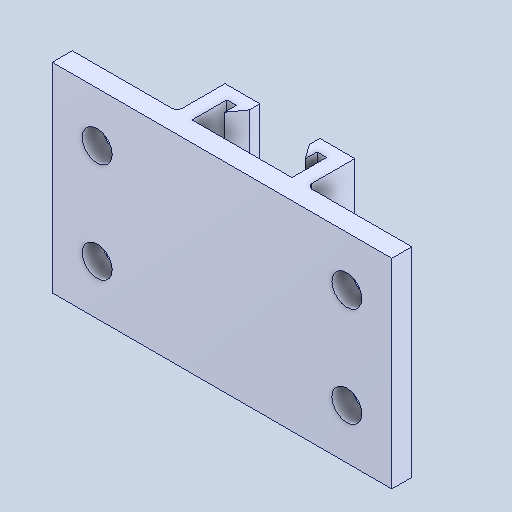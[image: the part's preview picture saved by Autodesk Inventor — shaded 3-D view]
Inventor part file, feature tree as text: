
AUTODESK INVENTOR PART (.ipt)
format: ipt  version: 2024.2 (Build 282272000, 272)  size: 220,160 bytes
history: native  units: in
note: dims shown in document units (in); Inventor stores cm internally (conversion verified against a paired STEP export)
features: fillet x1
ambient origin geometry x8: Origin, YZ Plane, XZ Plane, XY Plane, X Axis, Y Axis, Z Axis, Center Point
bodies: Solid1 (feature_tree)
feature tree (1):
  fillet  "Redondeo1"  [1 undecoded]
note: 1 required parameter value undecoded (feature->parameter linkage not recoverable at this tier; creation-order binding heuristic only, values carry confidence <= 0.55)
